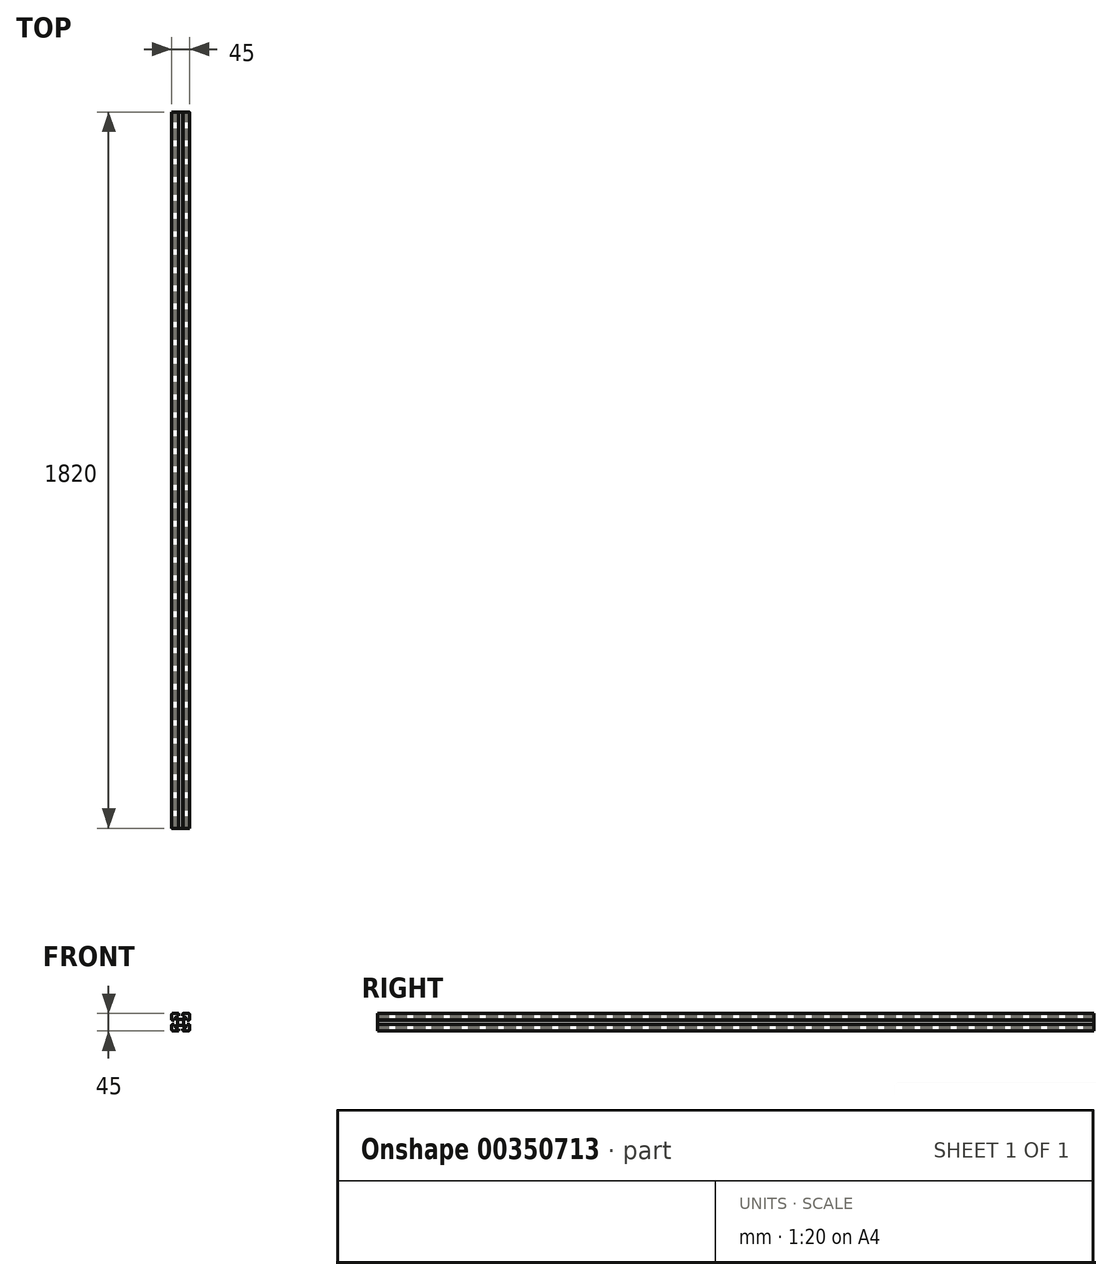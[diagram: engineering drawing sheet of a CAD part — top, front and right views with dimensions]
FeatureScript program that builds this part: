
annotation { "Feature Type Name" : "Feature", "Feature Type Description" : "" }
export const myFeature = defineFeature(function(context is Context, id is Id, definition is map)
    precondition{}
    {
        {
            var Q0;
            Q0=qCreatedBy(makeId("Front.planeOp"),FACE);
            var sketch = newSketch(context, id + "F0", { "sketchPlane" : qUnion([Q0])});
            skLineSegment(sketch, "E0", {"start": v(80.5, 122.5) * mm, "end": v(93.5, 122.5) * mm});
            skLineSegment(sketch, "E1", {"start": v(95, 121) * mm, "end": v(95, 116.5) * mm});
            skLineSegment(sketch, "E2", {"start": v(95, 116.5) * mm, "end": v(90, 116.5) * mm});
            skLineSegment(sketch, "E3", {"start": v(90, 116.5) * mm, "end": v(90, 112.5) * mm});
            skLineSegment(sketch, "E4", {"start": v(90, 112.5) * mm, "end": v(95, 107.5) * mm});
            skLineSegment(sketch, "E5", {"start": v(95, 107.5) * mm, "end": v(100, 107.5) * mm});
            skLineSegment(sketch, "E6", {"start": v(95, 121) * mm, "end": v(94.5, 121) * mm});
            skLineSegment(sketch, "E7", {"start": v(94.5, 121) * mm, "end": v(94.5, 121.5) * mm});
            skPoint(sketch, "E8.orphan", {"position": v(95, 122.5) * mm});
            skPoint(sketch, "E9.visualSharp", {"position": v(94.5, 122.5) * mm});
            skArc(sketch, "E9.filletArc", {"start": v(94.5, 121.5) * mm, "mid": v(94.2, 122.2) * mm, "end": v(93.5, 122.5) * mm});
            skPoint(sketch, "E10.visualSharp", {"position": v(77.5, 122.5) * mm});
            skArc(sketch, "E10.filletArc", {"start": v(80.5, 122.5) * mm, "mid": v(79.35, 122.27) * mm, "end": v(78.38, 121.62) * mm});
            skLineSegment(sketch, "E11.4", {"start": v(-7, 19.5) * mm, "end": v(-7, 19.5) * mm});
            skLineSegment(sketch, "E11.11", {"start": v(-19.5, 7) * mm, "end": v(-19.5, 7) * mm});
            skLineSegment(sketch, "E12", {"start": v(77.5, 122.5) * mm, "end": v(100, 100) * mm, "construction": true});
            skLineSegment(sketch, "E13.MirrorCS", {"start": v(92.5, 105) * mm, "end": v(92.5, 100) * mm});
            skLineSegment(sketch, "E14.MirrorCS", {"start": v(87.5, 110) * mm, "end": v(92.5, 105) * mm});
            skLineSegment(sketch, "E15.MirrorCS", {"start": v(83.5, 110) * mm, "end": v(87.5, 110) * mm});
            skLineSegment(sketch, "E16.MirrorCS", {"start": v(83.5, 105) * mm, "end": v(83.5, 110) * mm});
            skLineSegment(sketch, "E17.MirrorCS", {"start": v(79, 105) * mm, "end": v(83.5, 105) * mm});
            skLineSegment(sketch, "E18.MirrorCS", {"start": v(79, 105) * mm, "end": v(79, 105.5) * mm});
            skLineSegment(sketch, "E19.MirrorCS", {"start": v(79, 105.5) * mm, "end": v(78.5, 105.5) * mm});
            skArc(sketch, "E20.MirrorCS", {"start": v(78.5, 105.5) * mm, "mid": v(77.8, 105.8) * mm, "end": v(77.5, 106.5) * mm});
            skLineSegment(sketch, "E21.MirrorCS", {"start": v(77.5, 119.5) * mm, "end": v(77.5, 106.5) * mm});
            skArc(sketch, "E22.MirrorCS", {"start": v(77.5, 119.5) * mm, "mid": v(77.73, 120.65) * mm, "end": v(78.38, 121.62) * mm});
            skLineSegment(sketch, "E23.MirrorCS", {"start": v(105, 121) * mm, "end": v(105.5, 121) * mm});
            skLineSegment(sketch, "E24.MirrorCS", {"start": v(105.5, 121) * mm, "end": v(105.5, 121.5) * mm});
            skLineSegment(sketch, "E25.MirrorCS", {"start": v(121, 105.5) * mm, "end": v(121.5, 105.5) * mm});
            skLineSegment(sketch, "E26.MirrorCS", {"start": v(121, 105) * mm, "end": v(121, 105.5) * mm});
            skArc(sketch, "E27.MirrorCS", {"start": v(105.5, 121.5) * mm, "mid": v(105.8, 122.2) * mm, "end": v(106.5, 122.5) * mm});
            skLineSegment(sketch, "E28.MirrorCS", {"start": v(110, 116.5) * mm, "end": v(110, 112.5) * mm});
            skArc(sketch, "E29.MirrorCS", {"start": v(122.5, 119.5) * mm, "mid": v(122.27, 120.65) * mm, "end": v(121.62, 121.62) * mm});
            skLineSegment(sketch, "E30.MirrorCS", {"start": v(112.5, 110) * mm, "end": v(107.5, 105) * mm});
            skLineSegment(sketch, "E31.MirrorCS", {"start": v(110, 112.5) * mm, "end": v(105, 107.5) * mm});
            skPoint(sketch, "E32.MirrorP", {"position": v(105.5, 122.5) * mm});
            skLineSegment(sketch, "E33.MirrorCS", {"start": v(105, 116.5) * mm, "end": v(110, 116.5) * mm});
            skArc(sketch, "E34.MirrorCS", {"start": v(119.5, 122.5) * mm, "mid": v(120.65, 122.27) * mm, "end": v(121.62, 121.62) * mm});
            skLineSegment(sketch, "E35.MirrorCS", {"start": v(121, 105) * mm, "end": v(116.5, 105) * mm});
            skLineSegment(sketch, "E36.MirrorCS", {"start": v(122.5, 119.5) * mm, "end": v(122.5, 106.5) * mm});
            skArc(sketch, "E37.MirrorCS", {"start": v(121.5, 105.5) * mm, "mid": v(122.2, 105.8) * mm, "end": v(122.5, 106.5) * mm});
            skLineSegment(sketch, "E38.MirrorCS", {"start": v(107.5, 105) * mm, "end": v(107.5, 100) * mm});
            skLineSegment(sketch, "E39.MirrorCS", {"start": v(116.5, 110) * mm, "end": v(112.5, 110) * mm});
            skPoint(sketch, "E40.MirrorP", {"position": v(122.5, 122.5) * mm});
            skLineSegment(sketch, "E41.MirrorCS", {"start": v(122.5, 122.5) * mm, "end": v(100, 100) * mm, "construction": true});
            skLineSegment(sketch, "E42.MirrorCS", {"start": v(105, 121) * mm, "end": v(105, 116.5) * mm});
            skLineSegment(sketch, "E43.MirrorCS", {"start": v(116.5, 105) * mm, "end": v(116.5, 110) * mm});
            skLineSegment(sketch, "E44.MirrorCS", {"start": v(105, 107.5) * mm, "end": v(100, 107.5) * mm});
            skPoint(sketch, "E45.MirrorP", {"position": v(105, 122.5) * mm});
            skLineSegment(sketch, "E46.MirrorCS", {"start": v(119.5, 122.5) * mm, "end": v(106.5, 122.5) * mm});
            skLineSegment(sketch, "E47.MirrorCS", {"start": v(94.5, 79) * mm, "end": v(94.5, 78.5) * mm});
            skLineSegment(sketch, "E48.MirrorCS", {"start": v(79, 95) * mm, "end": v(79, 94.5) * mm});
            skLineSegment(sketch, "E49.MirrorCS", {"start": v(95, 92.5) * mm, "end": v(100, 92.5) * mm});
            skLineSegment(sketch, "E50.MirrorCS", {"start": v(79, 94.5) * mm, "end": v(78.5, 94.5) * mm});
            skLineSegment(sketch, "E51.MirrorCS", {"start": v(95, 79) * mm, "end": v(94.5, 79) * mm});
            skArc(sketch, "E52.MirrorCS", {"start": v(94.5, 78.5) * mm, "mid": v(94.2, 77.8) * mm, "end": v(93.5, 77.5) * mm});
            skLineSegment(sketch, "E53.MirrorCS", {"start": v(77.5, 80.5) * mm, "end": v(77.5, 93.5) * mm});
            skLineSegment(sketch, "E54.MirrorCS", {"start": v(83.5, 90) * mm, "end": v(87.5, 90) * mm});
            skPoint(sketch, "E55.MirrorP", {"position": v(95, 77.5) * mm});
            skLineSegment(sketch, "E56.MirrorCS", {"start": v(90, 83.5) * mm, "end": v(90, 87.5) * mm});
            skArc(sketch, "E57.MirrorCS", {"start": v(78.5, 94.5) * mm, "mid": v(77.8, 94.2) * mm, "end": v(77.5, 93.5) * mm});
            skLineSegment(sketch, "E58.MirrorCS", {"start": v(80.5, 77.5) * mm, "end": v(93.5, 77.5) * mm});
            skPoint(sketch, "E59.MirrorP", {"position": v(77.5, 77.5) * mm});
            skPoint(sketch, "E60.MirrorP", {"position": v(94.5, 77.5) * mm});
            skLineSegment(sketch, "E61.MirrorCS", {"start": v(87.5, 90) * mm, "end": v(92.5, 95) * mm});
            skLineSegment(sketch, "E62.MirrorCS", {"start": v(90, 87.5) * mm, "end": v(95, 92.5) * mm});
            skLineSegment(sketch, "E63.MirrorCS", {"start": v(95, 79) * mm, "end": v(95, 83.5) * mm});
            skLineSegment(sketch, "E64.MirrorCS", {"start": v(77.5, 77.5) * mm, "end": v(100, 100) * mm, "construction": true});
            skArc(sketch, "E65.MirrorCS", {"start": v(80.5, 77.5) * mm, "mid": v(79.35, 77.73) * mm, "end": v(78.38, 78.38) * mm});
            skArc(sketch, "E66.MirrorCS", {"start": v(77.5, 80.5) * mm, "mid": v(77.73, 79.35) * mm, "end": v(78.38, 78.38) * mm});
            skLineSegment(sketch, "E67.MirrorCS", {"start": v(83.5, 95) * mm, "end": v(83.5, 90) * mm});
            skLineSegment(sketch, "E68.MirrorCS", {"start": v(95, 83.5) * mm, "end": v(90, 83.5) * mm});
            skLineSegment(sketch, "E69.MirrorCS", {"start": v(79, 95) * mm, "end": v(83.5, 95) * mm});
            skLineSegment(sketch, "E70.MirrorCS", {"start": v(121, 95) * mm, "end": v(121, 94.5) * mm});
            skLineSegment(sketch, "E71.MirrorCS", {"start": v(105, 79) * mm, "end": v(105.5, 79) * mm});
            skLineSegment(sketch, "E72.MirrorCS", {"start": v(105.5, 79) * mm, "end": v(105.5, 78.5) * mm});
            skLineSegment(sketch, "E73.MirrorCS", {"start": v(121, 94.5) * mm, "end": v(121.5, 94.5) * mm});
            skArc(sketch, "E74.MirrorCS", {"start": v(105.5, 78.5) * mm, "mid": v(105.8, 77.8) * mm, "end": v(106.5, 77.5) * mm});
            skArc(sketch, "E75.MirrorCS", {"start": v(122.5, 80.5) * mm, "mid": v(122.27, 79.35) * mm, "end": v(121.62, 78.38) * mm});
            skLineSegment(sketch, "E76.MirrorCS", {"start": v(121, 95) * mm, "end": v(116.5, 95) * mm});
            skArc(sketch, "E77.MirrorCS", {"start": v(121.5, 94.5) * mm, "mid": v(122.2, 94.2) * mm, "end": v(122.5, 93.5) * mm});
            skLineSegment(sketch, "E78.MirrorCS", {"start": v(116.5, 90) * mm, "end": v(112.5, 90) * mm});
            skPoint(sketch, "E79.MirrorP", {"position": v(105, 77.5) * mm});
            skPoint(sketch, "E80.MirrorP", {"position": v(105.5, 77.5) * mm});
            skLineSegment(sketch, "E81.MirrorCS", {"start": v(105, 83.5) * mm, "end": v(110, 83.5) * mm});
            skPoint(sketch, "E82.MirrorP", {"position": v(122.5, 77.5) * mm});
            skLineSegment(sketch, "E83.MirrorCS", {"start": v(112.5, 90) * mm, "end": v(107.5, 95) * mm});
            skLineSegment(sketch, "E84.MirrorCS", {"start": v(110, 83.5) * mm, "end": v(110, 87.5) * mm});
            skLineSegment(sketch, "E85.MirrorCS", {"start": v(110, 87.5) * mm, "end": v(105, 92.5) * mm});
            skLineSegment(sketch, "E86.MirrorCS", {"start": v(116.5, 95) * mm, "end": v(116.5, 90) * mm});
            skArc(sketch, "E87.MirrorCS", {"start": v(119.5, 77.5) * mm, "mid": v(120.65, 77.73) * mm, "end": v(121.62, 78.38) * mm});
            skLineSegment(sketch, "E88.MirrorCS", {"start": v(119.5, 77.5) * mm, "end": v(106.5, 77.5) * mm});
            skLineSegment(sketch, "E89.MirrorCS", {"start": v(105, 79) * mm, "end": v(105, 83.5) * mm});
            skLineSegment(sketch, "E90.MirrorCS", {"start": v(122.5, 80.5) * mm, "end": v(122.5, 93.5) * mm});
            skLineSegment(sketch, "E91.MirrorCS", {"start": v(107.5, 95) * mm, "end": v(107.5, 100) * mm});
            skLineSegment(sketch, "E92.MirrorCS", {"start": v(105, 92.5) * mm, "end": v(100, 92.5) * mm});
            skLineSegment(sketch, "E93.MirrorCS", {"start": v(92.5, 95) * mm, "end": v(92.5, 100) * mm});
            skSolve(sketch);
        }
        {
            var Q0;
            Q0=qSketchRegion(id+"F0",true);
            extrude(context, id + "F1", {"entities" : qUnion([Q0]), "depth" : 1820 * mm});
        }
    });
